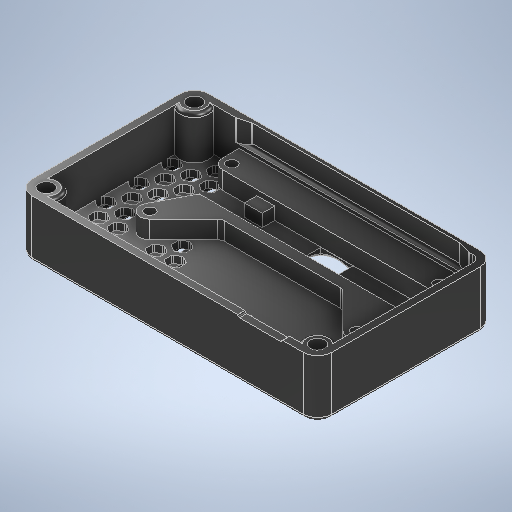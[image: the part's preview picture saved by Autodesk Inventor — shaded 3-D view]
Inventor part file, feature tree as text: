
AUTODESK INVENTOR PART (.ipt)
format: ipt  version: 2025 (Build 290162000, 162)  size: 2,141,184 bytes
history: native  units: mm
features: extrude x14, sketch x13, reference x9, fillet x8, projected_geometry x4, other x3, draft x1
ambient origin geometry x8: Origin, YZ Plane, XZ Plane, XY Plane, X Axis, Y Axis, Z Axis, Center Point
bodies: Solid1 (feature_tree)
feature tree (52):
  sketch  "Sketch1"  dims[d1=80.0mm d2=2.0mm]
  extrude  "Extrusion1"  Depth=2.0mm
  extrude  "Extrusion2"  Depth=2.0mm
  extrude  "Extrusion4"  Depth=9.1mm
  extrude  "Extrusion5"  Depth=2.0mm TaperAngle=0.0deg
  sketch  "Sketch2"  dims[d8=62.0mm d9=9.1mm]
  extrude  "Extrusion14"  Depth=12.0mm
  extrude  "Extrusion6"  Depth=5.0mm
  draft  "FaceDraft1"
  extrude  "Extrusion7"  Depth=10.0mm
  extrude  "Extrusion8"  Depth=2.0mm
  fillet  "Fillet6"  Radius=3.0mm
  fillet  "Fillet8"  Radius=2.0mm
  fillet  "Fillet9"  [1 undecoded]
  extrude  "Extrusion9"  Depth=5.0mm TaperAngle=0.0deg
  fillet  "Fillet10"  Radius=4.0mm
  extrude  "Extrusion11"  Depth=2.0mm
  fillet  "Fillet11"  Radius=2.0mm
  fillet  "Fillet12"  [1 undecoded]
  extrude  "Extrusion12"  Depth=2.0mm
  extrude  "Extrusion13"  TaperAngle=60.0deg  [1 undecoded]
  fillet  "Fillet13"  Radius=5.0mm
  extrude  "Extrusion15"  Depth=4.1mm
  fillet  "Fillet14"  Radius=7.0mm
  extrude  "Extrusion16"  Depth=4.1mm TaperAngle=0.0deg
  sketch  "Sketch Rectangular Pattern1"  dims[d3=2.0mm d4=2.9mm d5=58.0mm d6=23.0mm d7=5.5mm]
  projected_geometry  "Projected Loop2"
  sketch  "Sketch4"  dims[d10=9.0mm d11=2.0mm d12=0.0mm]
  sketch  "Sketch Rectangular Pattern6"  dims[d21=8.0mm d22=5.0mm]
  projected_geometry  "Projected Loop7"
  sketch  "Sketch5"  dims[d13=12.0mm d14=0.0mm d18=28.0mm]
  projected_geometry  "Projected Loop8"
  sketch  "Sketch Rectangular Pattern7"  dims[d32=2.0mm d33=4.0mm d34=3.0mm d35=2.0mm d36=135.0deg]
  sketch  "Sketch Rectangular Pattern8"  dims[d42=4.0mm d43=20.0mm d44=2.0mm d45=135.0deg]
  sketch  "Sketch Rectangular Pattern9"  dims[d51=2.0mm d52=0.0mm d54=60.0deg d55=5.0mm]
  sketch  "Sketch Rectangular Pattern10"  dims[d82=3.5mm d83=5.0mm d84=7.0mm d85=3.5mm d86=0.0mm d87=8.0mm d88=0.0mm d89=0.5mm d91=2.0mm d92=1.0mm d93=3.5mm d94=15.0mm d95=49.5mm d96=45.5mm d97=2.9mm d99=7.0mm d100=0.0mm d101=1.0mm d137=110.0mm d139=5.0mm d140=10.0mm d142=10.0mm d144=10.0mm d145=0.0mm d146=3.0mm d147=2.0mm d148=1.0mm d149=0.5mm d150=4.0mm d151=0.5mm d152=30.0mm d154=5.333333mm d155=10.0mm d157=10.0mm d159=40.0mm d161=5.333333mm d162=10.0mm d164=10.0mm d166=50.0mm d168=5.333333mm d169=10.0mm d171=10.0mm d173=90.0mm d175=5.333333mm d176=10.0mm d178=10.0mm d180=2.0mm d181=0.0mm d182=2.0mm d183=0.0mm d184=1.0mm d185=0.0mm d186=0.5mm d187=1.0mm d188=15.0deg d189=15.0deg d190=6.0mm d191=0.0mm d192=1.0mm d193=4.1mm d194=4.1mm d195=0.0mm d90=0.0mm]
  sketch  "Sketch6"  dims[d23=50.0mm d25=6.0mm d26=10.0mm d28=10.0mm d31=13.0mm]
  reference  "Reference1"
  reference  "Reference2"
  reference  "Reference3"
  reference  "Reference4"
  reference  "Reference5"
  reference  "Reference6"
  reference  "Reference7"
  reference  "Reference8"
  reference  "Reference9"
  sketch  "Sketch7"  dims[d37=135.0deg d38=5.0mm d39=0.0mm d40=4.0mm d41=0.0mm]
  projected_geometry  "Projected Loop9"
  sketch  "Sketch8"  dims[d46=135.0deg d50=2.0mm]
  parser-record x1  (decoder bookkeeping rows leaked as tree rows — omitted from the tree; the rows remain in map.json)
  other  "RemoteCameraModule.iam"
  other  "RemoteCasingBackCover:1"
note: 3 required parameter values undecoded (feature->parameter linkage not recoverable at this tier; creation-order binding heuristic only, values carry confidence <= 0.55)
note: 1 file-system path scrubbed to <path> (originals preserved in map.json)
